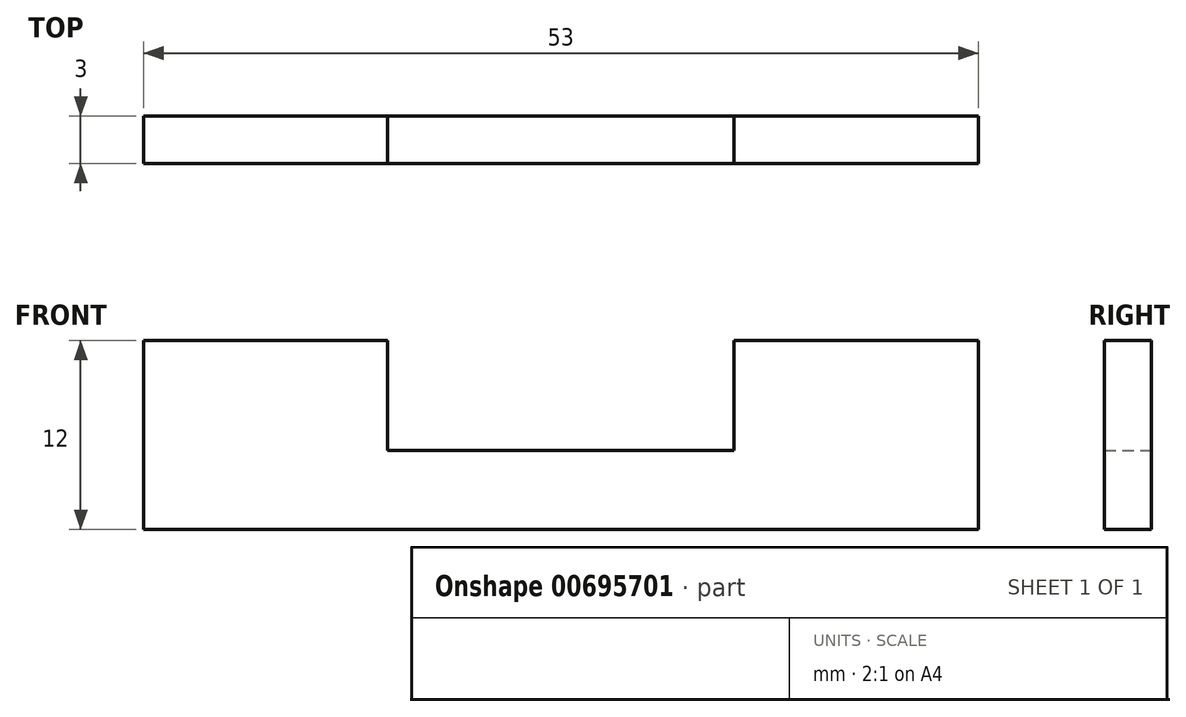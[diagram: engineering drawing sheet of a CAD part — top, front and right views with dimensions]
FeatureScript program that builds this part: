
annotation { "Feature Type Name" : "Feature", "Feature Type Description" : "" }
export const myFeature = defineFeature(function(context is Context, id is Id, definition is map)
    precondition{}
    {
        {
            var Q0;
            Q0=qCreatedBy(makeId("Front.planeOp"),FACE);
            var sketch = newSketch(context, id + "F0", { "sketchPlane" : qUnion([Q0])});
            skLineSegment(sketch, "E0.bottom", {"start": v(-26.5, 6) * mm, "end": v(-11, 6) * mm});
            skLineSegment(sketch, "E0.top", {"start": v(-26.5, -6) * mm, "end": v(26.5, -6) * mm});
            skLineSegment(sketch, "E0.left", {"start": v(-26.5, 6) * mm, "end": v(-26.5, -6) * mm});
            skLineSegment(sketch, "E0.right", {"start": v(26.5, 6) * mm, "end": v(26.5, -6) * mm});
            skLineSegment(sketch, "E1.top", {"start": v(-11, -1) * mm, "end": v(11, -1) * mm});
            skLineSegment(sketch, "E1.left", {"start": v(-11, 6) * mm, "end": v(-11, -1) * mm});
            skLineSegment(sketch, "E1.right", {"start": v(11, 6) * mm, "end": v(11, -1) * mm});
            skLineSegment(sketch, "E2.trimOffspring", {"start": v(11, 6) * mm, "end": v(26.5, 6) * mm});
            skSolve(sketch);
        }
        {
            var Q0;
            Q0 = qSketchRegion(id + "F0", true);
            extrude(context, id + "F1", {"entities" : qUnion([Q0]), "depth" : 3 * mm, "offsetDistance" : 25 * mm});
        }
    });
